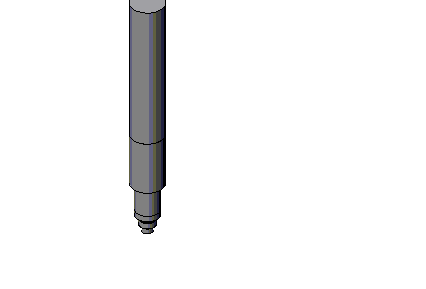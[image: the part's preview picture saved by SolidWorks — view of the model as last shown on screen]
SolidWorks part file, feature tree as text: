
SOLIDWORKS PART (.sldprt)
format: sldprt  version: not decoded by parser v0  size: 98,304 bytes
history: native  units: mm
features: sketch x8, extrude x8 (+10 scaffold rows collapsed)
feature tree (26):
  scaffold x10  (default folders/planes/origin — collapsed)
  sketch  "Sketch1"  dims[D1=11.1125mm]
  extrude  "Extrude1"  Depth=6.35mm
  sketch  "Sketch2"  dims[D1=0.0mm]
  extrude  "Extrude2"  Depth=1.5875mm
  sketch  "Sketch3"  dims[D1=17.4625mm]
  extrude  "Extrude3"  Depth=6.35mm
  sketch  "Sketch4"  dims[D1=0.0mm]
  extrude  "Extrude4"  Depth=4.7625mm
  sketch  "Sketch5"  dims[D1=25.4mm]
  extrude  "Extrude5"  Depth=6.35mm
  sketch  "Sketch6"  dims[D1=0.0mm]
  extrude  "Extrude6"  Depth=30.1625mm
  sketch  "Sketch7"  dims[D1=34.925mm]
  extrude  "Extrude7"  Depth=57.15mm
  sketch  "Sketch8"  dims[D1=0.0mm]
  extrude  "Extrude8"  Depth=152.4mm
decode coverage: 16 of 16 modeling features carry decoded parameters
note: suppression state not decoded; provenance and decode notes live in map.json
